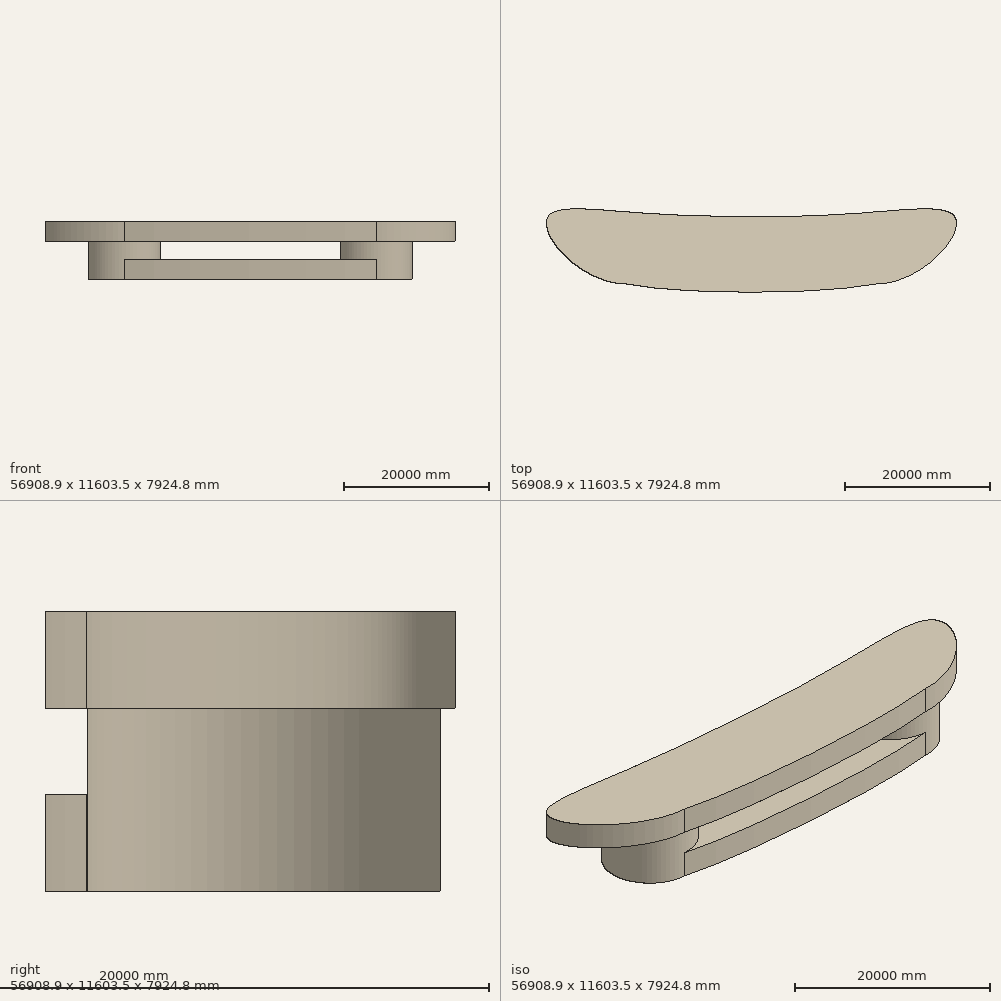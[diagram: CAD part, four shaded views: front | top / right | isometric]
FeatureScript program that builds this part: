
annotation { "Feature Type Name" : "Feature", "Feature Type Description" : "" }
export const myFeature = defineFeature(function(context is Context, id is Id, definition is map)
    precondition{}
    {
        {
            var Q0;
            Q0=qCreatedBy(makeId("Top.planeOp"),FACE);
            var sketch = newSketch(context, id + "F0", { "sketchPlane" : qUnion([Q0])});
            skCircle(sketch, "E0", {"center": v(0, 0) * mm, "radius": 5000 * mm});
            skCircle(sketch, "E1", {"center": v(35000, 0) * mm, "radius": 5000 * mm});
            skFitSpline(sketch, "E2", {"points": [v(0, 5000) * mm, v(35000, 5000) * mm], "startDerivative": vector(25507.18, -2526.27) * mm, "endDerivative": vector(27647.56, 3011.72) * mm});
            skFitSpline(sketch, "E3", {"points": [v(0, -5000) * mm, v(35000, -5000) * mm], "startDerivative": vector(24293.56, -4808.72) * mm, "endDerivative": vector(23763.95, 4566) * mm});
            skFitSpline(sketch, "E4", {"points": [v(35000, 5000) * mm, v(45280.56, 4732.51) * mm, v(44420.95, 0) * mm, v(35000, -5000) * mm], "startDerivative": vector(18938.27, 739.96) * mm, "endDerivative": vector(-26991.66, 0) * mm});
            skLineSegment(sketch, "E5", {"start": v(0, 0) * mm, "end": v(35000, 0) * mm});
            skLineSegment(sketch, "E6", {"start": v(17500, 0) * mm, "end": v(17500, -2617.59) * mm});
            skFitSpline(sketch, "E7.MirrorCS", {"points": [v(0, 5000) * mm, v(-10280.56, 4732.51) * mm, v(-9420.95, 0) * mm, v(0, -5000) * mm], "startDerivative": vector(-18938.27, 739.96) * mm, "endDerivative": vector(26991.66, 0) * mm});
            skSolve(sketch);
        }
        {
            var Q0;
            {var subQ0=sQuery(id+"F0.wireOp",EDGE,"E2");var subQ1=sQuery(id+"F0.wireOp",EDGE,"E0");var subQ2=makeQuery(id+"F0.imprint","INTERSECT",VERTEX,{"derivedFrom":[subQ1,subQ0]});Q0=makeQuery(id+"F0.imprint","IMPRINT",FACE,{"disambiguationData":[TD([[makeQuery(id+"F0.imprint","IMPRINT",EDGE,{"disambiguationData":[TD([[subQ2,1.0]])],"derivedFrom":subQ1}),1.0]])]});}
            var Q1;
            {var subQ0=sQuery(id+"F0.wireOp",EDGE,"E2");var subQ1=sQuery(id+"F0.wireOp",EDGE,"E1");var subQ2=makeQuery(id+"F0.imprint","INTERSECT",VERTEX,{"derivedFrom":[subQ1,subQ0]});Q1=makeQuery(id+"F0.imprint","IMPRINT",FACE,{"disambiguationData":[TD([[makeQuery(id+"F0.imprint","IMPRINT",EDGE,{"disambiguationData":[TD([[subQ2,-1.0]])],"derivedFrom":subQ1}),1.0]])]});}
            extrude(context, id + "F1", {"entities" : qUnion([Q0, Q1]), "depth" : 5181.6 * mm});
        }
        {
            var Q0;
            {var subQ4=sQuery(id+"F0.wireOp",EDGE,"E3");Q0=makeQuery(id+"F0.imprint","IMPRINT",FACE,{"disambiguationData":[TD([[makeQuery(id+"F0.imprint","IMPRINT",EDGE,{"derivedFrom":subQ4}),1.0]])]});}
            var Q1;
            {var subQ0=sQuery(id+"F0.wireOp",EDGE,"E5");var subQ1=makeQuery(id+"F0.imprint","IMPRINT",VERTEX,{"derivedFrom":subQ0});Q1=makeQuery(id+"F0.imprint","IMPRINT",FACE,{"disambiguationData":[TD([[makeQuery(id+"F0.imprint","IMPRINT",EDGE,{"disambiguationData":[TD([[subQ1,1.0]])],"derivedFrom":subQ0}),1.0]])]});}
            extrude(context, id + "F2", {"entities" : qUnion([Q0, Q1]), "depth" : 2743.2 * mm});
        }
        {
            var Q0;
            {var subQ0=sQuery(id+"F0.wireOp",EDGE,"E7.MirrorCS");Q0=makeQuery(id+"F0.imprint","IMPRINT",FACE,{"disambiguationData":[TD([[makeQuery(id+"F0.imprint","IMPRINT",EDGE,{"derivedFrom":subQ0}),1.0]])]});}
            var Q1;
            {var subQ0=sQuery(id+"F0.wireOp",EDGE,"E5");var subQ1=makeQuery(id+"F0.imprint","IMPRINT",VERTEX,{"derivedFrom":subQ0});Q1=makeQuery(id+"F0.imprint","IMPRINT",FACE,{"disambiguationData":[TD([[makeQuery(id+"F0.imprint","IMPRINT",EDGE,{"disambiguationData":[TD([[subQ1,1.0]])],"derivedFrom":subQ0}),1.0]])]});}
            var Q2;
            {var subQ4=sQuery(id+"F0.wireOp",EDGE,"E3");Q2=makeQuery(id+"F0.imprint","IMPRINT",FACE,{"disambiguationData":[TD([[makeQuery(id+"F0.imprint","IMPRINT",EDGE,{"derivedFrom":subQ4}),1.0]])]});}
            var Q3;
            {var subQ0=sQuery(id+"F0.wireOp",EDGE,"E4");Q3=makeQuery(id+"F0.imprint","IMPRINT",FACE,{"disambiguationData":[TD([[makeQuery(id+"F0.imprint","IMPRINT",EDGE,{"derivedFrom":subQ0}),-1.0]])]});}
            var Q4;
            {var subQ0=sQuery(id+"F0.wireOp",EDGE,"E2");var subQ1=sQuery(id+"F0.wireOp",EDGE,"E1");var subQ3=makeQuery(id+"F0.imprint","INTERSECT",VERTEX,{"derivedFrom":[subQ1,subQ0]});Q4=makeQuery(id+"F0.imprint","IMPRINT",FACE,{"disambiguationData":[TD([[makeQuery(id+"F0.imprint","IMPRINT",EDGE,{"disambiguationData":[TD([[subQ3,1.0]])],"derivedFrom":subQ1}),1.0]])]});}
            var Q5;
            {var subQ0=sQuery(id+"F0.wireOp",EDGE,"E2");var subQ1=sQuery(id+"F0.wireOp",EDGE,"E1");var subQ2=makeQuery(id+"F0.imprint","INTERSECT",VERTEX,{"derivedFrom":[subQ1,subQ0]});Q5=makeQuery(id+"F0.imprint","IMPRINT",FACE,{"disambiguationData":[TD([[makeQuery(id+"F0.imprint","IMPRINT",EDGE,{"disambiguationData":[TD([[subQ2,-1.0]])],"derivedFrom":subQ1}),1.0]])]});}
            var Q6;
            {var subQ0=sQuery(id+"F0.wireOp",EDGE,"E2");var subQ1=sQuery(id+"F0.wireOp",EDGE,"E0");var subQ3=makeQuery(id+"F0.imprint","INTERSECT",VERTEX,{"derivedFrom":[subQ1,subQ0]});Q6=makeQuery(id+"F0.imprint","IMPRINT",FACE,{"disambiguationData":[TD([[makeQuery(id+"F0.imprint","IMPRINT",EDGE,{"disambiguationData":[TD([[subQ3,-1.0]])],"derivedFrom":subQ1}),1.0]])]});}
            var Q7;
            {var subQ0=sQuery(id+"F0.wireOp",EDGE,"E2");var subQ1=sQuery(id+"F0.wireOp",EDGE,"E0");var subQ2=makeQuery(id+"F0.imprint","INTERSECT",VERTEX,{"derivedFrom":[subQ1,subQ0]});Q7=makeQuery(id+"F0.imprint","IMPRINT",FACE,{"disambiguationData":[TD([[makeQuery(id+"F0.imprint","IMPRINT",EDGE,{"disambiguationData":[TD([[subQ2,1.0]])],"derivedFrom":subQ1}),1.0]])]});}
            extrude(context, id + "F3", {"entities" : qUnion([Q0, Q1, Q2, Q3, Q4, Q5, Q6, Q7]), "depth" : 7924.8 * mm, "hasSecondDirection" : true, "secondDirectionOppositeDirection" : false, "secondDirectionDepth" : 5181.6 * mm});
        }
    });
